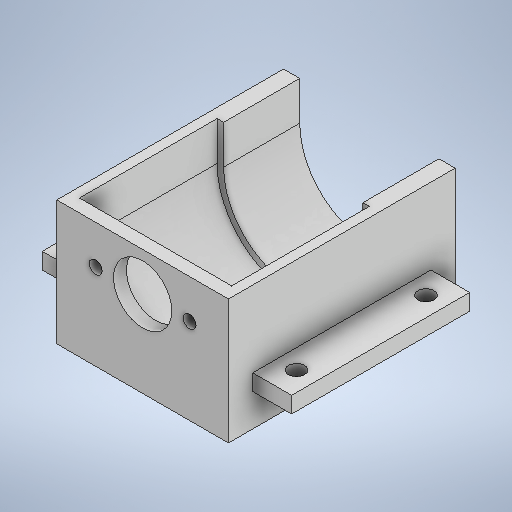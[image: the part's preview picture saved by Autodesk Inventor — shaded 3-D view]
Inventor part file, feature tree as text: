
AUTODESK INVENTOR PART (.ipt)
format: ipt  version: 2025.3 (Build 293356000, 356)  size: 647,168 bytes
history: native  units: mm
features: extrude x4, projected_geometry x3, other x2, sketch x2
ambient origin geometry x8: Origin, YZ Plane, XZ Plane, XY Plane, X Axis, Y Axis, Z Axis, Center Point
bodies: Body1 (feature_tree)
feature tree (11):
  other  "솔리드1"
  sketch  "스케치1"
  extrude  "돌출1"  Depth=47.0mm
  extrude  "돌출2"  Depth=3.0mm
  extrude  "돌출3"  Depth=3.0mm
  other  "작업 평면1"
  extrude  "돌출6"  Depth=3.0mm
  sketch  "스케치2"
  projected_geometry  "투영된 루프1"
  projected_geometry  "투영된 루프2"
  projected_geometry  "투영된 루프3"
